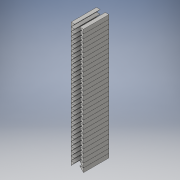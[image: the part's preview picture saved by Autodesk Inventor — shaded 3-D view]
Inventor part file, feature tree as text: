
AUTODESK INVENTOR PART (.ipt)
format: ipt  version: 2016 (Build 200138000, 138)  size: 218,624 bytes
history: native  units: in
note: dims shown in document units (in); Inventor stores cm internally (conversion verified against a paired STEP export)
features: extrude x1, pattern_linear x1, sketch x1
ambient origin geometry x8: Origin, YZ Plane, XZ Plane, XY Plane, X Axis, Y Axis, Z Axis, Center Point
bodies: Solid1 (feature_tree)
feature tree (3):
  extrude  "Extrusion1"  Depth=0.025in
  pattern_linear  "Rectangular Pattern1"  Spacing1=0.0375in  [1 undecoded]
  sketch  "Sketch1"  dims[d0=0.0247in d1=0.025in d2=0.0375in d3=0.0223in d4=0.154in d5=0.0in d6=11.811in d8=0.025in]
note: 1 required parameter value undecoded (feature->parameter linkage not recoverable at this tier; creation-order binding heuristic only, values carry confidence <= 0.55)
